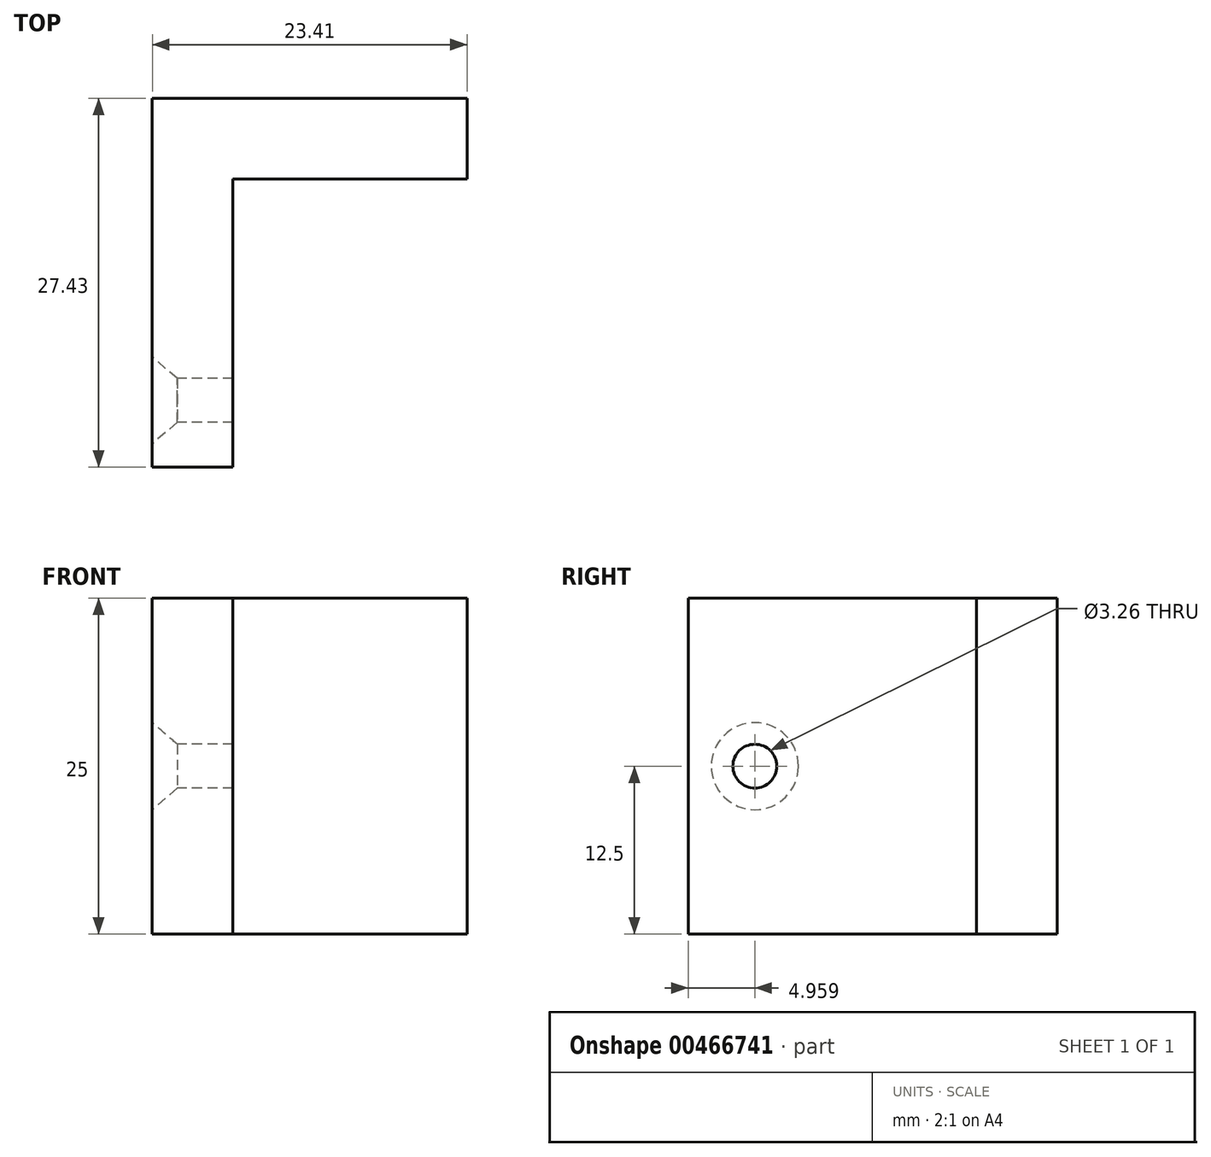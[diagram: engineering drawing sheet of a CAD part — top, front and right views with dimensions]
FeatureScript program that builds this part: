
annotation { "Feature Type Name" : "Feature", "Feature Type Description" : "" }
export const myFeature = defineFeature(function(context is Context, id is Id, definition is map)
    precondition{}
    {
        {
            var Q0;
            Q0=qCreatedBy(makeId("Top.planeOp"),FACE);
            var sketch = newSketch(context, id + "F0", { "sketchPlane" : qUnion([Q0])});
            skLineSegment(sketch, "E0", {"start": v(-29, -21.43) * mm, "end": v(-29, 6) * mm});
            skLineSegment(sketch, "E1", {"start": v(-29, 6) * mm, "end": v(-5.6, 6) * mm});
            skLineSegment(sketch, "E2", {"start": v(-5.6, 6) * mm, "end": v(-5.6, 0) * mm});
            skLineSegment(sketch, "E3", {"start": v(-5.6, 0) * mm, "end": v(-23, 0) * mm});
            skLineSegment(sketch, "E4", {"start": v(-23, 0) * mm, "end": v(-23, -21.43) * mm});
            skLineSegment(sketch, "E5", {"start": v(-29, -21.43) * mm, "end": v(-23, -21.43) * mm});
            skSolve(sketch);
        }
        {
            var Q0;
            Q0=makeQuery(id+"F0.imprint","IMPRINT",FACE,{"disambiguationData":[TD([[makeQuery(id+"F0.imprint","IMPRINT",EDGE,{"derivedFrom":sQuery(id+"F0.wireOp",EDGE,"E0")}),-1.0]])]});
            extrude(context, id + "F1", {"entities" : qUnion([Q0]), "depth" : 25 * mm, "offsetDistance" : 25 * mm});
        }
        {
            var Q0;
            Q0=makeQuery(id+"F1.opExtrude","SWEPT_FACE",FACE,{"disambiguationData":[OSD([sQuery(id+"F0.wireOp",EDGE,"E0")])]});
            var sketch = newSketch(context, id + "F2", { "sketchPlane" : qUnion([Q0])});
            skLineSegment(sketch, "E6", {"start": v(7.71, 0) * mm, "end": v(7.71, 25) * mm});
            skLineSegment(sketch, "E7", {"start": v(7.71, 0) * mm, "end": v(21.43, 0) * mm});
            skLineSegment(sketch, "E8", {"start": v(11.52, 0) * mm, "end": v(11.52, 25) * mm});
            skLineSegment(sketch, "E9", {"start": v(11.52, 25) * mm, "end": v(21.43, 0) * mm});
            skLineSegment(sketch, "E10", {"start": v(11.52, 0) * mm, "end": v(21.43, 25) * mm});
            skPoint(sketch, "E11", {"position": v(16.47, 12.5) * mm});
            skSolve(sketch);
        }
        {
            var Q0;
            Q0=sQuery(id+"F2.wireOp",VERTEX,"E11");
            var Q1;
            Q1=makeQuery(id+"F1.opExtrude","SWEPT_BODY",BODY,{"disambiguationData":[OSD([sQuery(id+"F0.wireOp",EDGE,"E0"),sQuery(id+"F0.wireOp",EDGE,"E1"),sQuery(id+"F0.wireOp",EDGE,"E2"),sQuery(id+"F0.wireOp",EDGE,"E3"),sQuery(id+"F0.wireOp",EDGE,"E4"),sQuery(id+"F0.wireOp",EDGE,"E5")])]});
            hole(context, id + "F3", {"style" : HoleStyle.C_SINK, "endStyle" : HoleEndStyle.THROUGH, "standardTappedOrClearance" : lookupTablePath({ "standard" : "ANSI", "fit" : "Normal (ASME)", "size" : "#4", "type" : "Clearance" }), "standardBlindInLast" : lookupTablePath({ "fit" : "Free", "standard" : "ANSI", "size" : "#4", "type" : "Clearance" }), "holeDiameter" : 3.26 * mm, "cSinkDiameter" : 6.48 * mm, "cSinkAngle" : 82 * degree, "majorDiameter" : 5 * mm, "isTappedThrough" : true, "tappedDepth" : 12 * mm, "tapClearance" : 3, "locations" : qUnion([Q0]), "scope" : qUnion([Q1])});
        }
    });
